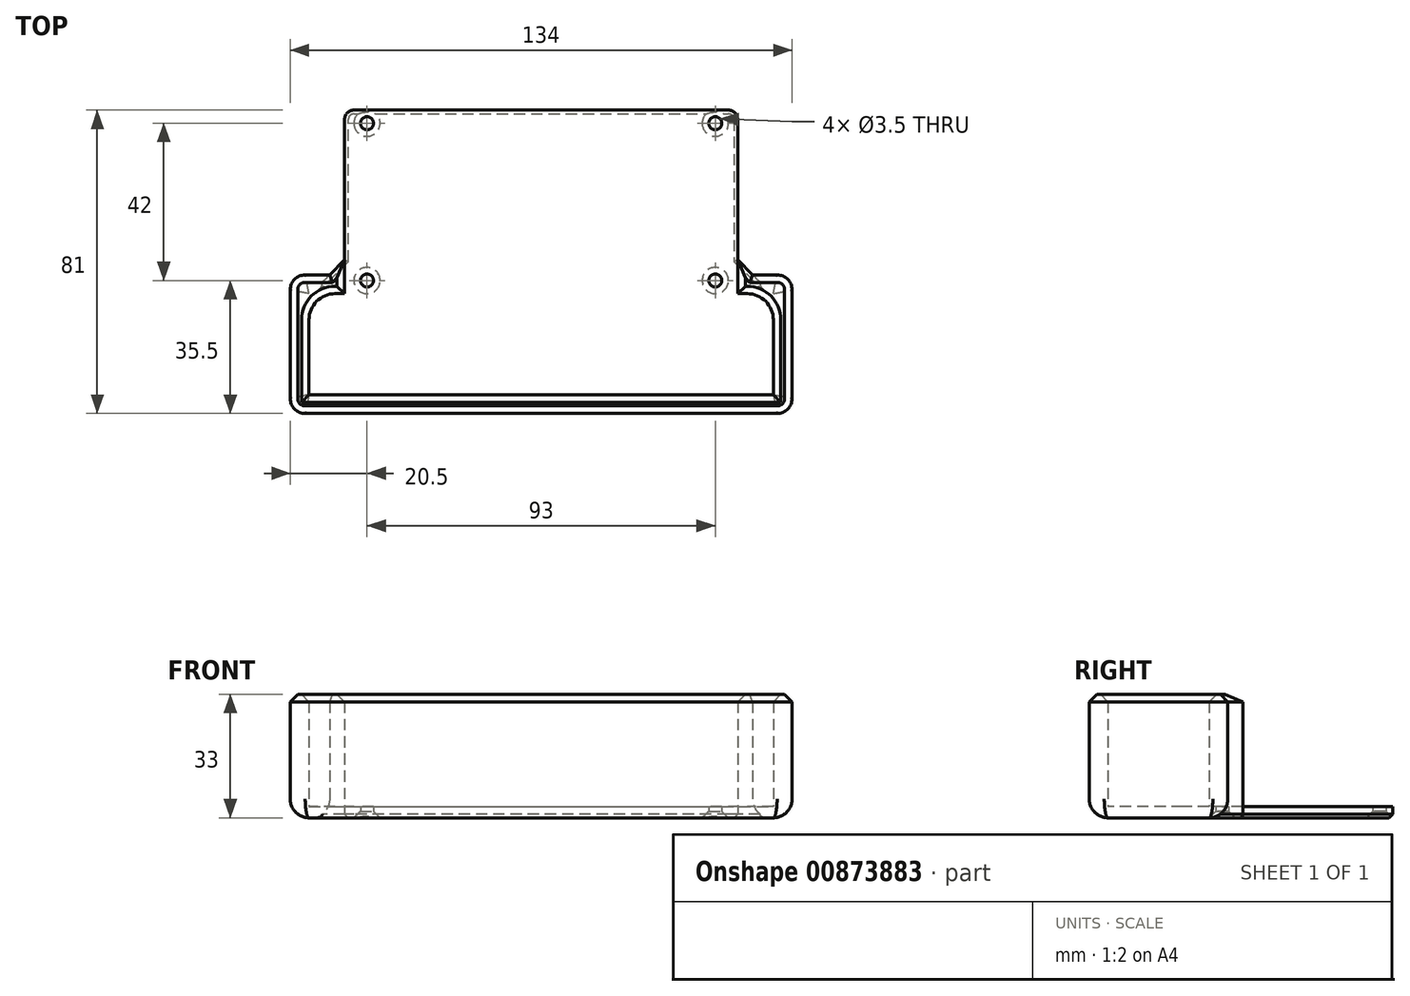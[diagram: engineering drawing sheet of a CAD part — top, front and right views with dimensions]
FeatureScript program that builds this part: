
annotation { "Feature Type Name" : "Feature", "Feature Type Description" : "" }
export const myFeature = defineFeature(function(context is Context, id is Id, definition is map)
    precondition{}
    {
        {
            var Q0;
            Q0=qCreatedBy(makeId("Top.planeOp"),FACE);
            var sketch = newSketch(context, id + "F0", { "sketchPlane" : qUnion([Q0])});
            skLineSegment(sketch, "E0.bottom", {"start": v(0, 0) * mm, "end": v(105, 0) * mm});
            skLineSegment(sketch, "E0.top", {"start": v(2.5, 49) * mm, "end": v(102.5, 49) * mm});
            skLineSegment(sketch, "E0.left", {"start": v(0, 9) * mm, "end": v(0, 46.5) * mm});
            skLineSegment(sketch, "E0.right", {"start": v(105, 9) * mm, "end": v(105, 46.5) * mm});
            skLineSegment(sketch, "E1.bottom", {"start": v(-9.5, 0) * mm, "end": v(114.5, 0) * mm});
            skLineSegment(sketch, "E1.top", {"start": v(-9.5, -27) * mm, "end": v(114.5, -27) * mm});
            skLineSegment(sketch, "E1.left", {"start": v(-9.5, 0) * mm, "end": v(-9.5, -27) * mm});
            skLineSegment(sketch, "E1.right", {"start": v(114.5, 0) * mm, "end": v(114.5, -27) * mm});
            skLineSegment(sketch, "E2.0", {"start": v(-14.5, 1) * mm, "end": v(-14.5, -28) * mm});
            skLineSegment(sketch, "E2.1", {"start": v(-10.5, 5) * mm, "end": v(-4, 5) * mm});
            skLineSegment(sketch, "E2.2", {"start": v(119.5, 1) * mm, "end": v(119.5, -28) * mm});
            skLineSegment(sketch, "E2.3", {"start": v(-10.5, -32) * mm, "end": v(115.5, -32) * mm});
            skLineSegment(sketch, "E3.trimOffspring", {"start": v(109, 5) * mm, "end": v(115.5, 5) * mm});
            skPoint(sketch, "E4.visualSharp", {"position": v(0, 49) * mm});
            skArc(sketch, "E4.filletArc", {"start": v(2.5, 49) * mm, "mid": v(0.73, 48.27) * mm, "end": v(0, 46.5) * mm});
            skPoint(sketch, "E5.visualSharp", {"position": v(105, 49) * mm});
            skArc(sketch, "E5.filletArc", {"start": v(105, 46.5) * mm, "mid": v(104.27, 48.27) * mm, "end": v(102.5, 49) * mm});
            skPoint(sketch, "E6.visualSharp", {"position": v(0, 5) * mm});
            skPoint(sketch, "E7.visualSharp", {"position": v(105, 5) * mm});
            skPoint(sketch, "E8.visualSharp", {"position": v(-14.5, 5) * mm});
            skArc(sketch, "E8.filletArc", {"start": v(-10.5, 5) * mm, "mid": v(-13.33, 3.83) * mm, "end": v(-14.5, 1) * mm});
            skPoint(sketch, "E9.visualSharp", {"position": v(119.5, 5) * mm});
            skArc(sketch, "E9.filletArc", {"start": v(119.5, 1) * mm, "mid": v(118.33, 3.83) * mm, "end": v(115.5, 5) * mm});
            skPoint(sketch, "E10.visualSharp", {"position": v(-14.5, -32) * mm});
            skArc(sketch, "E10.filletArc", {"start": v(-14.5, -28) * mm, "mid": v(-13.33, -30.83) * mm, "end": v(-10.5, -32) * mm});
            skPoint(sketch, "E11.visualSharp", {"position": v(119.5, -32) * mm});
            skArc(sketch, "E11.filletArc", {"start": v(115.5, -32) * mm, "mid": v(118.33, -30.83) * mm, "end": v(119.5, -28) * mm});
            skLineSegment(sketch, "E12", {"start": v(-4, 5) * mm, "end": v(0, 9) * mm});
            skLineSegment(sketch, "E13", {"start": v(105, 9) * mm, "end": v(109, 5) * mm});
            skSolve(sketch);
        }
        {
            var Q0;
            Q0 = qSketchRegion(id + "F0", true);
            var Q1;
            Q1=makeQuery(id+"F0.imprint","IMPRINT",FACE,{"disambiguationData":[TD([[makeQuery(id+"F0.imprint","IMPRINT",EDGE,{"derivedFrom":sQuery(id+"F0.wireOp",EDGE,"E1.top")}),1.0]])]});
            extrude(context, id + "F1", {"entities" : qUnion([Q0, Q1]), "depth" : 3 * mm, "offsetDistance" : 25 * mm});
        }
        {
            var Q0;
            Q0=makeQuery(id+"F1.opExtrude","CAP_FACE",FACE,{"disambiguationData":[OSD([sQuery(id+"F0.wireOp",EDGE,"E0.top"),sQuery(id+"F0.wireOp",EDGE,"E0.left"),sQuery(id+"F0.wireOp",EDGE,"E0.right"),sQuery(id+"F0.wireOp",EDGE,"E2.0"),sQuery(id+"F0.wireOp",EDGE,"E2.1"),sQuery(id+"F0.wireOp",EDGE,"E2.2"),sQuery(id+"F0.wireOp",EDGE,"E2.3"),sQuery(id+"F0.wireOp",EDGE,"E3.trimOffspring"),sQuery(id+"F0.wireOp",EDGE,"E4.filletArc"),sQuery(id+"F0.wireOp",EDGE,"E5.filletArc"),sQuery(id+"F0.wireOp",EDGE,"E6.filletArc"),sQuery(id+"F0.wireOp",EDGE,"E7.filletArc"),sQuery(id+"F0.wireOp",EDGE,"E8.filletArc"),sQuery(id+"F0.wireOp",EDGE,"E9.filletArc"),sQuery(id+"F0.wireOp",EDGE,"E10.filletArc"),sQuery(id+"F0.wireOp",EDGE,"E11.filletArc")])],"isStart":false});
            var sketch = newSketch(context, id + "F2", { "sketchPlane" : qUnion([Q0])});
            skLineSegment(sketch, "E14.0", {"start": v(-9.5, -7) * mm, "end": v(-9.5, -27) * mm});
            skLineSegment(sketch, "E15.0", {"start": v(-2.5, 0) * mm, "end": v(107.5, 0) * mm});
            skArc(sketch, "E16.0.0", {"start": v(-14.5, -28) * mm, "mid": v(-13.33, -30.83) * mm, "end": v(-10.5, -32) * mm});
            skLineSegment(sketch, "E16.0.1", {"start": v(-10.5, -32) * mm, "end": v(115.5, -32) * mm});
            skArc(sketch, "E16.0.2", {"start": v(115.5, -32) * mm, "mid": v(118.33, -30.83) * mm, "end": v(119.5, -28) * mm});
            skLineSegment(sketch, "E16.0.3", {"start": v(119.5, -28) * mm, "end": v(119.5, 1) * mm});
            skArc(sketch, "E16.0.4", {"start": v(119.5, 1) * mm, "mid": v(118.33, 3.83) * mm, "end": v(115.5, 5) * mm});
            skLineSegment(sketch, "E16.0.5", {"start": v(115.5, 5) * mm, "end": v(109, 5) * mm});
            skLineSegment(sketch, "E16.0.7", {"start": v(105, 9) * mm, "end": v(105, 46.5) * mm});
            skArc(sketch, "E16.0.8", {"start": v(105, 46.5) * mm, "mid": v(104.27, 48.27) * mm, "end": v(102.5, 49) * mm});
            skLineSegment(sketch, "E16.0.9", {"start": v(102.5, 49) * mm, "end": v(2.5, 49) * mm});
            skArc(sketch, "E16.0.10", {"start": v(2.5, 49) * mm, "mid": v(0.73, 48.27) * mm, "end": v(0, 46.5) * mm});
            skLineSegment(sketch, "E16.0.11", {"start": v(0, 46.5) * mm, "end": v(0, 9) * mm});
            skLineSegment(sketch, "E16.0.13", {"start": v(-10.5, 5) * mm, "end": v(-10.5, 5) * mm});
            skArc(sketch, "E16.0.14", {"start": v(-10.5, 5) * mm, "mid": v(-13.33, 3.83) * mm, "end": v(-14.5, 1) * mm});
            skLineSegment(sketch, "E16.0.15", {"start": v(-14.5, 1) * mm, "end": v(-14.5, -28) * mm});
            skLineSegment(sketch, "E17.0", {"start": v(-9.5, -27) * mm, "end": v(114.5, -27) * mm});
            skLineSegment(sketch, "E18.0", {"start": v(114.5, -7) * mm, "end": v(114.5, -27) * mm});
            skLineSegment(sketch, "E19", {"start": v(0, 33.24) * mm, "end": v(0, 0) * mm});
            skLineSegment(sketch, "E20", {"start": v(105, 25) * mm, "end": v(105, 0) * mm});
            skPoint(sketch, "E21.visualSharp", {"position": v(-9.5, 0) * mm});
            skArc(sketch, "E21.filletArc", {"start": v(-2.5, 0) * mm, "mid": v(-7.45, -2.05) * mm, "end": v(-9.5, -7) * mm});
            skPoint(sketch, "E22.visualSharp", {"position": v(114.5, 0) * mm});
            skArc(sketch, "E22.filletArc", {"start": v(114.5, -7) * mm, "mid": v(112.45, -2.05) * mm, "end": v(107.5, 0) * mm});
            skLineSegment(sketch, "E23.0", {"start": v(105, 9) * mm, "end": v(109, 5) * mm});
            skLineSegment(sketch, "E24.0.6", {"start": v(109, 5) * mm, "end": v(105, 9) * mm});
            skLineSegment(sketch, "E24.0.12", {"start": v(0, 9) * mm, "end": v(-4, 5) * mm});
            skLineSegment(sketch, "E24.0.13", {"start": v(-4, 5) * mm, "end": v(-10.5, 5) * mm});
            skSolve(sketch);
        }
        {
            var Q0;
            Q0=makeQuery(id+"F2.imprint","IMPRINT",FACE,{"disambiguationData":[TD([[makeQuery(id+"F2.imprint","IMPRINT",EDGE,{"derivedFrom":sQuery(id+"F2.wireOp",EDGE,"E14.0")}),-1.0]])]});
            extrude(context, id + "F3", {"entities" : qUnion([Q0]), "operationType" : NewBodyOperationType.ADD, "depth" : 30 * mm, "offsetDistance" : 25 * mm});
        }
        {
            var Q0;
            Q0=makeQuery(id+"F3.opExtrude","CAP_EDGE",EDGE,{"disambiguationData":[OSD([sQuery(id+"F2.wireOp",EDGE,"E16.0.15")])],"isStart":false});
            var Q1;
            Q1=makeQuery(id+"F3.opExtrude","CAP_EDGE",EDGE,{"disambiguationData":[OSD([sQuery(id+"F2.wireOp",EDGE,"E16.0.0")])],"isStart":false});
            var Q2;
            Q2=makeQuery(id+"F3.opExtrude","CAP_EDGE",EDGE,{"disambiguationData":[OSD([sQuery(id+"F2.wireOp",EDGE,"E16.0.1")])],"isStart":false});
            var Q3;
            Q3=makeQuery(id+"F3.opExtrude","CAP_EDGE",EDGE,{"disambiguationData":[OSD([sQuery(id+"F2.wireOp",EDGE,"E16.0.3")])],"isStart":false});
            var Q4;
            Q4=makeQuery(id+"F3.opExtrude","CAP_EDGE",EDGE,{"disambiguationData":[OSD([sQuery(id+"F2.wireOp",EDGE,"E16.0.2")])],"isStart":false});
            var Q5;
            Q5=makeQuery(id+"F3.opExtrude","CAP_EDGE",EDGE,{"disambiguationData":[OSD([sQuery(id+"F2.wireOp",EDGE,"E16.0.5")])],"isStart":false});
            var Q6;
            Q6=makeQuery(id+"F3.opExtrude","CAP_EDGE",EDGE,{"disambiguationData":[OSD([sQuery(id+"F2.wireOp",EDGE,"E24.0.6")])],"isStart":false});
            var Q7;
            Q7=makeQuery(id+"F3.opExtrude","CAP_EDGE",EDGE,{"disambiguationData":[OSD([sQuery(id+"F2.wireOp",EDGE,"E16.0.4")])],"isStart":false});
            var Q8;
            Q8=makeQuery(id+"F3.opExtrude","CAP_EDGE",EDGE,{"disambiguationData":[OSD([sQuery(id+"F2.wireOp",EDGE,"E20")])],"isStart":false});
            var Q9;
            Q9=makeQuery(id+"F3.opExtrude","CAP_FACE",FACE,{"disambiguationData":[OSD([sQuery(id+"F2.wireOp",EDGE,"E14.0"),sQuery(id+"F2.wireOp",EDGE,"E15.0"),sQuery(id+"F2.wireOp",EDGE,"E17.0"),sQuery(id+"F2.wireOp",EDGE,"E18.0"),sQuery(id+"F2.wireOp",EDGE,"E19"),sQuery(id+"F2.wireOp",EDGE,"E20"),sQuery(id+"F2.wireOp",EDGE,"E21.filletArc"),sQuery(id+"F2.wireOp",EDGE,"E22.filletArc"),sQuery(id+"F2.wireOp",EDGE,"E16.0.0"),sQuery(id+"F2.wireOp",EDGE,"E16.0.1"),sQuery(id+"F2.wireOp",EDGE,"E16.0.2"),sQuery(id+"F2.wireOp",EDGE,"E16.0.3"),sQuery(id+"F2.wireOp",EDGE,"E16.0.4"),sQuery(id+"F2.wireOp",EDGE,"E16.0.5"),sQuery(id+"F2.wireOp",EDGE,"E24.0.6"),sQuery(id+"F2.wireOp",EDGE,"E24.0.12"),sQuery(id+"F2.wireOp",EDGE,"E24.0.13"),sQuery(id+"F2.wireOp",EDGE,"E16.0.14"),sQuery(id+"F2.wireOp",EDGE,"E16.0.15")])],"isStart":false});
            chamfer(context, id + "F4", {"entities" : qUnion([Q0, Q1, Q2, Q3, Q4, Q5, Q6, Q7, Q8, Q9]), "width" : 2 * mm, "tangentPropagation" : true});
        }
        {
            var Q0;
            Q0=makeQuery(id+"F0.imprint","IMPRINT",FACE,{"disambiguationData":[TD([[makeQuery(id+"F0.imprint","IMPRINT",EDGE,{"derivedFrom":sQuery(id+"F0.wireOp",EDGE,"E0.top")}),-1.0]])]});
            var sketch = newSketch(context, id + "F5", { "sketchPlane" : qUnion([Q0])});
            skPoint(sketch, "E25", {"position": v(6, 3.5) * mm});
            skPoint(sketch, "E26", {"position": v(6, 45.5) * mm});
            skPoint(sketch, "E27", {"position": v(99, 45.5) * mm});
            skPoint(sketch, "E28", {"position": v(99, 3.5) * mm});
            skSolve(sketch);
        }
        {
            var Q0;
            Q0=sQuery(id+"F5.wireOp",VERTEX,"E26");
            var Q1;
            Q1=sQuery(id+"F5.wireOp",VERTEX,"E25");
            var Q2;
            Q2=sQuery(id+"F5.wireOp",VERTEX,"E27");
            var Q3;
            Q3=sQuery(id+"F5.wireOp",VERTEX,"E28");
            var Q4;
            Q4=makeQuery(id+"F1.opExtrude","SWEPT_BODY",BODY,{"disambiguationData":[OSD([sQuery(id+"F0.wireOp",EDGE,"E0.top"),sQuery(id+"F0.wireOp",EDGE,"E0.left"),sQuery(id+"F0.wireOp",EDGE,"E0.right"),sQuery(id+"F0.wireOp",EDGE,"E2.0"),sQuery(id+"F0.wireOp",EDGE,"E2.1"),sQuery(id+"F0.wireOp",EDGE,"E2.2"),sQuery(id+"F0.wireOp",EDGE,"E2.3"),sQuery(id+"F0.wireOp",EDGE,"E3.trimOffspring"),sQuery(id+"F0.wireOp",EDGE,"E4.filletArc"),sQuery(id+"F0.wireOp",EDGE,"E5.filletArc"),sQuery(id+"F0.wireOp",EDGE,"E8.filletArc"),sQuery(id+"F0.wireOp",EDGE,"E9.filletArc"),sQuery(id+"F0.wireOp",EDGE,"E10.filletArc"),sQuery(id+"F0.wireOp",EDGE,"E11.filletArc"),sQuery(id+"F0.wireOp",EDGE,"E12"),sQuery(id+"F0.wireOp",EDGE,"E13")])]});
            hole(context, id + "F6", {"style" : HoleStyle.C_SINK, "endStyle" : HoleEndStyle.THROUGH, "oppositeDirection" : true, "holeDiameter" : 3.5 * mm, "cSinkDiameter" : 7 * mm, "cSinkAngle" : 90 * degree, "majorDiameter" : 5 * mm, "isTappedThrough" : true, "tappedDepth" : 12 * mm, "tapClearance" : 3, "locations" : qUnion([Q0, Q1, Q2, Q3]), "scope" : qUnion([Q4])});
        }
        {
            var Q0;
            Q0=makeQuery(id+"F1.opExtrude","CAP_EDGE",EDGE,{"disambiguationData":[OSD([sQuery(id+"F0.wireOp",EDGE,"E2.0")])],"isStart":true});
            var Q1;
            Q1=makeQuery(id+"F1.opExtrude","CAP_EDGE",EDGE,{"disambiguationData":[OSD([sQuery(id+"F0.wireOp",EDGE,"E10.filletArc")])],"isStart":true});
            var Q2;
            Q2=makeQuery(id+"F1.opExtrude","CAP_EDGE",EDGE,{"disambiguationData":[OSD([sQuery(id+"F0.wireOp",EDGE,"E2.3")])],"isStart":true});
            fillet(context, id + "F7", {"entities" : qUnion([Q0, Q1, Q2]), "radius" : 5 * mm, "tangentPropagation" : true, "allowEdgeOverflow" : false});
        }
        {
            var Q0;
            Q0=makeQuery(id+"F1.opExtrude","CAP_EDGE",EDGE,{"disambiguationData":[OSD([sQuery(id+"F0.wireOp",EDGE,"E12")])],"isStart":true});
            var Q1;
            Q1=makeQuery(id+"F1.opExtrude","CAP_EDGE",EDGE,{"disambiguationData":[OSD([sQuery(id+"F0.wireOp",EDGE,"E0.left")])],"isStart":true});
            var Q2;
            Q2=makeQuery(id+"F1.opExtrude","CAP_EDGE",EDGE,{"disambiguationData":[OSD([sQuery(id+"F0.wireOp",EDGE,"E4.filletArc")])],"isStart":true});
            var Q3;
            {var subQ0=sQuery(id+"F0.wireOp",EDGE,"E0.top");var subQ2=sQuery(id+"F0.wireOp",EDGE,"E5.filletArc");var subQ4=makeQuery(id+"F6.hole-0.opRevolve","SWEPT_FACE",FACE,{"disambiguationData":[OSD([sQuery(id+"F6.hole-0.sketch.wireOp",EDGE,"csink_start_line_1")])]});Q3=makeQuery(id+"F6.hole-2.boolean.opBoolean","SPLIT",EDGE,{"disambiguationData":[TD([makeQuery(id+"F6.hole-0.boolean.opBoolean","COPY",FACE,{"derivedFrom":subQ4})])],"derivedFrom":makeQuery(id+"F6.hole-0.boolean.opBoolean","SPLIT",EDGE,{"disambiguationData":[TD([makeQuery(id+"F1.opExtrude","SWEPT_FACE",FACE,{"disambiguationData":[OSD([subQ2])]})])],"derivedFrom":makeQuery(id+"F1.opExtrude","CAP_EDGE",EDGE,{"disambiguationData":[OSD([subQ0])],"isStart":true})})});}
            var Q4;
            {var subQ0=sQuery(id+"F0.wireOp",EDGE,"E0.top");var subQ1=sQuery(id+"F0.wireOp",EDGE,"E4.filletArc");Q4=makeQuery(id+"F6.hole-0.boolean.opBoolean","SPLIT",EDGE,{"disambiguationData":[TD([makeQuery(id+"F1.opExtrude","SWEPT_FACE",FACE,{"disambiguationData":[OSD([subQ1])]})])],"derivedFrom":makeQuery(id+"F1.opExtrude","CAP_EDGE",EDGE,{"disambiguationData":[OSD([subQ0])],"isStart":true})});}
            var Q5;
            Q5=makeQuery(id+"F1.opExtrude","CAP_EDGE",EDGE,{"disambiguationData":[OSD([sQuery(id+"F0.wireOp",EDGE,"E13")])],"isStart":true});
            var Q6;
            Q6=makeQuery(id+"F1.opExtrude","CAP_EDGE",EDGE,{"disambiguationData":[OSD([sQuery(id+"F0.wireOp",EDGE,"E0.right")])],"isStart":true});
            var Q7;
            Q7=makeQuery(id+"F1.opExtrude","CAP_EDGE",EDGE,{"disambiguationData":[OSD([sQuery(id+"F0.wireOp",EDGE,"E5.filletArc")])],"isStart":true});
            var Q8;
            {var subQ0=sQuery(id+"F0.wireOp",EDGE,"E0.top");var subQ2=sQuery(id+"F0.wireOp",EDGE,"E5.filletArc");var subQ4=makeQuery(id+"F1.opExtrude","SWEPT_FACE",FACE,{"disambiguationData":[OSD([subQ2])]});Q8=makeQuery(id+"F6.hole-2.boolean.opBoolean","SPLIT",EDGE,{"disambiguationData":[TD([subQ4])],"derivedFrom":makeQuery(id+"F6.hole-0.boolean.opBoolean","SPLIT",EDGE,{"disambiguationData":[TD([subQ4])],"derivedFrom":makeQuery(id+"F1.opExtrude","CAP_EDGE",EDGE,{"disambiguationData":[OSD([subQ0])],"isStart":true})})});}
            chamfer(context, id + "F8", {"entities" : qUnion([Q0, Q1, Q2, Q3, Q4, Q5, Q6, Q7, Q8]), "width" : 1 * mm, "tangentPropagation" : true});
        }
    });
